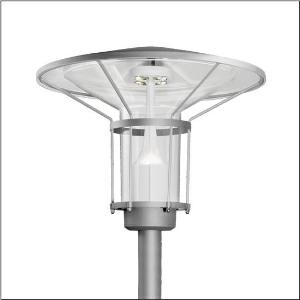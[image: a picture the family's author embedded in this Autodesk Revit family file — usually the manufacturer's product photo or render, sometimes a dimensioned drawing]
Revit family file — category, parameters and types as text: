
# Revit family: laterne_classic_iq___st1_2a_5xa5245ef14h_7fcb
name_source: partatom
category: Lighting Fixtures
units: mm (PartAtom-declared; Revit-internal decimal feet)

## family parameters
Cut with Voids When Loaded = No
Host = Face
Light Source = No
Part Type = Normal
Room Calculation Point = No
Round Connector Dimension = Use Diameter
Shared = No

## types (1)
- --- (1 x LED, 1380 lm, 10.5 W, 3000K)
    Apparent Load = 11 VA
    CIE Flux Codes = 21 60 93 97 100
    Color Rendering = 70
    Color Temperature = 3000K
    Default Elevation = 1800 mm
    Description = Lantern Classic iQ, mast luminaire, Module 540 iQ-SR, primary light control with 3 zone facetted reflector, of plastic, silver coated, highly specular, structured, primary optical cover: cover, of PMMA, transparent, light distribution: ST1.2a, light emission: direct distribution, primary light characteristic: asymmetric, installation type: post-top, LED, High Power LED, rated luminous flux: 1.380lm, luminous efficacy: 131lm/W, light colour: 730, colour temperature: 3000K, control gear: ECG iQ, control: Auto-Match, Temp-Guard, Lumen-Switch, Night-Set, Smart-Wire, Light-Fading, Desk-Remote (wireless, voltage-free reading and setting of iQ features in the workshop via application-optimized NFC function/RFID function), optimised constant luminous flux control (CLO 2.0), Street-Remote, presetting dimming logarithmic, with terminal, 6-pole, max. 2.5mm², mains connection: 230..240V, AC, 50/60Hz, start of lifetime: 11W, end of service life: 11W, reduction: 5W, luminaire housing, upper part, of glass-fibre reinforced polyester, coated, Siteco® metallic grey (DB 702S), diameter: 750mm, height: 596mm, spigot size: d x l = 76 x 70mm (post-top) | with reducer (optional accessory) 60 x 70mm, post-top mast mounting element, of diecast aluminium, coated, Siteco® metallic grey (DB 702S), Module 540 iQ-SR, traffic white (RAL 9016), equipment: standard, protection rating (complete): IP65, insulation class (complete): insulation class II (safety insulation), certification: CE, ENEC, VDE, packaging unit: 1 piece

Light Distribution: ST1.2a
    Height = 596 mm
    Lamp = 1 x LED
    Lamp Light Flux = 1380 lm
    Lamp Power = 10.5 W
    Lamp count = 1
    Length = 750 mm
    Luminous efficacy = 131 lm/W
    Manufacturer = Siteco
    ModVariant = No
    Model = 5XA5245EF14H
    Number of Poles = 1
    OnlyDefault = Yes
    Power Factor = 1
    Product Name = Laterne Classic iQ | ST1.2a
    Product group = mast luminaire | pylon top
    ProductGroupID = 6100
    Protection Class = Protection class II
    Protection Degree = IP 65
    RLX_Detail_Level = 1
    RLX_Emergency_Light_Flux = 0 lm
    RLX_Emergency_Type = 0
    RLX_Emergency_Type_DB = No
    RlxData = <blob elided: 91781 chars, md5=daf7257a>
    Socket = socket
    Standby Power = 0 W
    System Light Flux = 1380 lm
    System Power = 11 W
    Type Comments = factory setting: luminous flux: 100 % | dim-lin: 254 | 419 mA
    Type Image = l_1006052.jpg
    URL = http://relux.com
    VarID = @adj_110551
    Voltage = 0 V
    Weight = 0.00 kg
    Width = 0 mm  [stored 0 ft]

note: [stored X ft] marks values corroborated as IEEE doubles in the binary element streams (Revit-internal decimal feet)

## geometry (parser evidence)
native form markers: Blend x4, Sweep x11
no freeform markers — native parametric forms only
